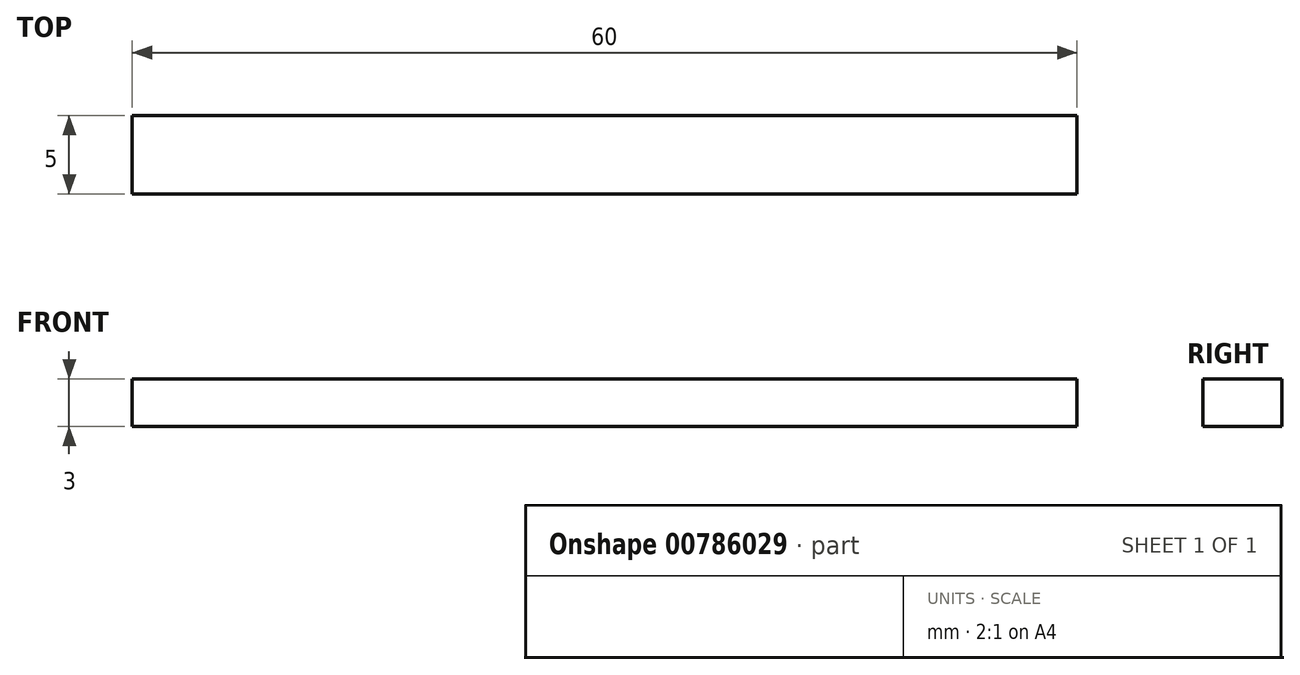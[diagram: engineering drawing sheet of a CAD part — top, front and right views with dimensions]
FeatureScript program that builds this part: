
annotation { "Feature Type Name" : "Feature", "Feature Type Description" : "" }
export const myFeature = defineFeature(function(context is Context, id is Id, definition is map)
    precondition{}
    {
        {
            var Q0;
            Q0=qCreatedBy(makeId("Front.planeOp"),FACE);
            var sketch = newSketch(context, id + "F0", { "sketchPlane" : qUnion([Q0])});
            skLineSegment(sketch, "E0.bottom", {"start": v(0, 0) * mm, "end": v(60, 0) * mm});
            skLineSegment(sketch, "E0.top", {"start": v(0, 3) * mm, "end": v(60, 3) * mm});
            skLineSegment(sketch, "E0.left", {"start": v(0, 0) * mm, "end": v(0, 3) * mm});
            skLineSegment(sketch, "E0.right", {"start": v(60, 0) * mm, "end": v(60, 3) * mm});
            skSolve(sketch);
        }
        {
            var Q0;
            Q0=qSketchRegion(id+"F0",true);
            extrude(context, id + "F1", {"entities" : qUnion([Q0]), "depth" : 5 * mm, "offsetDistance" : 25 * mm});
        }
    });
